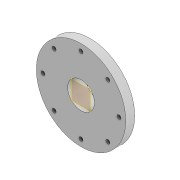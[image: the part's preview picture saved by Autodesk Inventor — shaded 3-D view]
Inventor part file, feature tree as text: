
AUTODESK INVENTOR PART (.ipt)
format: ipt  version: 2020.3 (Build 243373010, 373A)  size: 130,048 bytes
history: native  units: mm
features: sketch x4, extrude x3, hole x1, plane x1, projected_geometry x1
ambient origin geometry x8: Origin, YZ Plane, XZ Plane, XY Plane, X Axis, Y Axis, Z Axis, Center Point
bodies: Solid1 (feature_tree)
feature tree (10):
  sketch  "Sketch1"  dims[d0=100.0mm d2=80.0mm d3=95.0mm d4=85.0mm d5=360.0deg]
  extrude  "Extrusion1"  Depth=80.0mm TaperAngle=360.0deg
  hole  "Hole1"  [1 undecoded]
  sketch  "Sketch2"  dims[d6=10.0mm d7=0.0mm]
  plane  "Work Plane1"
  extrude  "Extrusion4"  Depth=10.0mm TaperAngle=0.0deg
  extrude  "Extrusion5"  Depth=10.0mm
  sketch  "Sketch4"  dims[d8=4.458734mm d9=10.0mm d10=6.0mm d11=2.0mm d12=90.0deg d13=10.0mm d14=20.594885mm d15=42.0mm]
  projected_geometry  "Projected Loop1"
  sketch  "Sketch5"  dims[d16=30.0mm d21=5.975mm d22=0.0mm d23=25.0mm d24=65.0mm d25=10.0mm d26=0.0mm]
note: 1 required parameter value undecoded (feature->parameter linkage not recoverable at this tier; creation-order binding heuristic only, values carry confidence <= 0.55)
